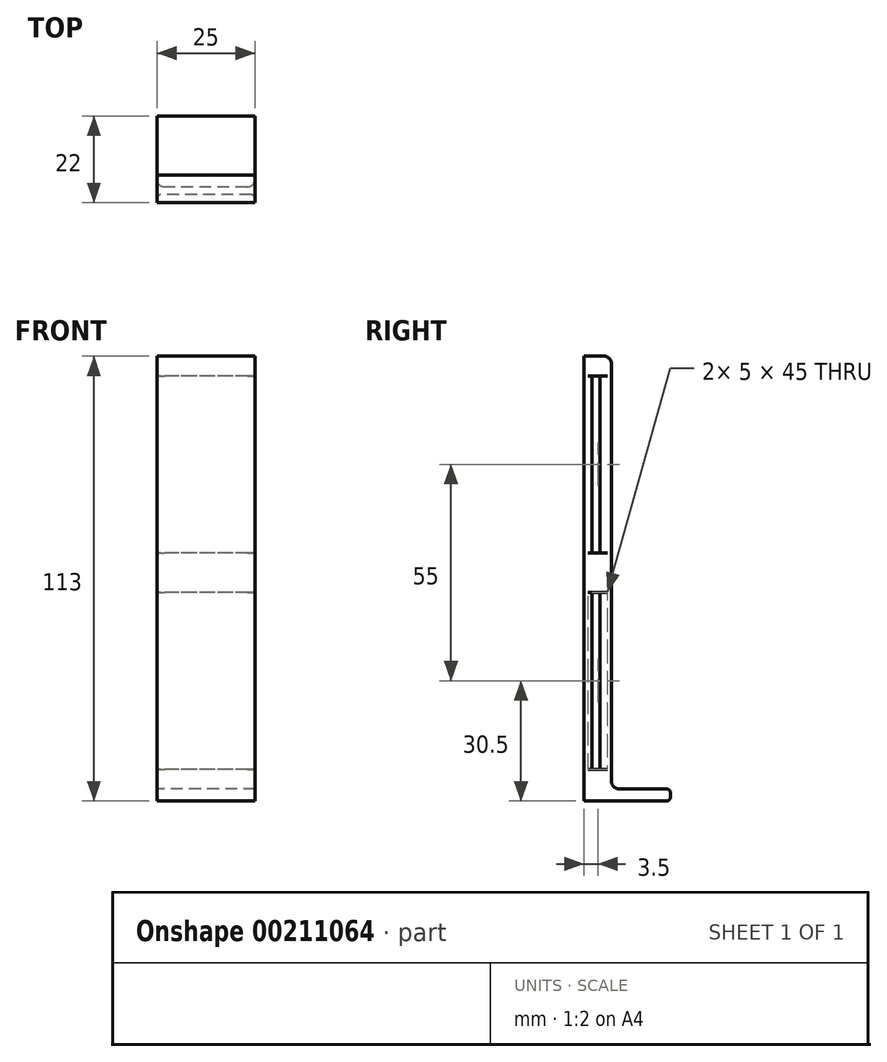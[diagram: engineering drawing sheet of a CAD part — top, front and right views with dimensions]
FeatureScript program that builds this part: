
annotation { "Feature Type Name" : "Feature", "Feature Type Description" : "" }
export const myFeature = defineFeature(function(context is Context, id is Id, definition is map)
    precondition{}
    {
        {
            var Q0;
            Q0=qCreatedBy(makeId("Right.planeOp"),FACE);
            var sketch = newSketch(context, id + "F0", { "sketchPlane" : qUnion([Q0])});
            skLineSegment(sketch, "E0", {"start": v(0, 113) * mm, "end": v(0, 0) * mm});
            skLineSegment(sketch, "E1", {"start": v(0, 0) * mm, "end": v(21, 0) * mm});
            skLineSegment(sketch, "E2", {"start": v(21, 3) * mm, "end": v(7, 3) * mm});
            skLineSegment(sketch, "E3", {"start": v(7, 3) * mm, "end": v(7, 113) * mm});
            skLineSegment(sketch, "E4", {"start": v(7, 113) * mm, "end": v(0, 113) * mm});
            skLineSegment(sketch, "E5.bottom", {"start": v(2, 108) * mm, "end": v(4, 108) * mm});
            skLineSegment(sketch, "E5.top", {"start": v(2, 63) * mm, "end": v(4, 63) * mm});
            skLineSegment(sketch, "E5.left", {"start": v(2, 108) * mm, "end": v(2, 63) * mm});
            skLineSegment(sketch, "E5.right", {"start": v(4, 108) * mm, "end": v(4, 63) * mm});
            skLineSegment(sketch, "E6.bottom", {"start": v(2, 53) * mm, "end": v(4, 53) * mm});
            skLineSegment(sketch, "E6.top", {"start": v(2, 8) * mm, "end": v(4, 8) * mm});
            skLineSegment(sketch, "E6.left", {"start": v(2, 53) * mm, "end": v(2, 8) * mm});
            skLineSegment(sketch, "E6.right", {"start": v(4, 53) * mm, "end": v(4, 8) * mm});
            skLineSegment(sketch, "E7", {"start": v(7, 58) * mm, "end": v(0, 58) * mm, "construction": true});
            skLineSegment(sketch, "E8", {"start": v(22, 1) * mm, "end": v(22, 2) * mm});
            skPoint(sketch, "E9.visualSharp", {"position": v(22, 3) * mm});
            skArc(sketch, "E9.filletArc", {"start": v(22, 2) * mm, "mid": v(21.7, 2.7) * mm, "end": v(21, 3) * mm});
            skPoint(sketch, "E10.visualSharp", {"position": v(22, 0) * mm});
            skArc(sketch, "E10.filletArc", {"start": v(21, 0) * mm, "mid": v(21.7, 0.3) * mm, "end": v(22, 1) * mm});
            skSolve(sketch);
        }
        {
            var Q0;
            Q0=makeQuery(id+"F0.imprint","IMPRINT",FACE,{"disambiguationData":[TD([[makeQuery(id+"F0.imprint","IMPRINT",EDGE,{"derivedFrom":sQuery(id+"F0.wireOp",EDGE,"E0")}),1.0]])]});
            extrude(context, id + "F1", {"entities" : qUnion([Q0]), "depth" : 25 * mm});
        }
        {
            var Q0;
            Q0=makeQuery(id+"F1.opExtrude","SWEPT_EDGE",EDGE,{"disambiguationData":[OSD([sQuery(id+"F0.wireOp",EDGE,"E2"),sQuery(id+"F0.wireOp",EDGE,"E3")])]});
            var Q1;
            Q1=makeQuery(id+"F1.opExtrude","SWEPT_EDGE",EDGE,{"disambiguationData":[OSD([sQuery(id+"F0.wireOp",EDGE,"TeItDx5S-dmeC-bbpO-K6b3-K9wIp6qIZ5ub"),sQuery(id+"F0.wireOp",EDGE,"E2")])]});
            var Q2;
            Q2=makeQuery(id+"F1.opExtrude","SWEPT_EDGE",EDGE,{"disambiguationData":[OSD([sQuery(id+"F0.wireOp",EDGE,"E3"),sQuery(id+"F0.wireOp",EDGE,"E4")])]});
            fillet(context, id + "F2", {"entities" : qUnion([Q0, Q1, Q2]), "radius" : 2 * mm, "tangentPropagation" : true, "allowEdgeOverflow" : false});
        }
        {
            var Q0;
            Q0=makeQuery(id+"F1.opExtrude","CAP_EDGE",EDGE,{"disambiguationData":[OSD([sQuery(id+"F0.wireOp",EDGE,"E5.right")])],"isStart":true});
            var Q1;
            Q1=makeQuery(id+"F1.opExtrude","CAP_EDGE",EDGE,{"disambiguationData":[OSD([sQuery(id+"F0.wireOp",EDGE,"E6.right")])],"isStart":true});
            var Q2;
            Q2=makeQuery(id+"F1.opExtrude","CAP_EDGE",EDGE,{"disambiguationData":[OSD([sQuery(id+"F0.wireOp",EDGE,"E6.right")])],"isStart":false});
            var Q3;
            Q3=makeQuery(id+"F1.opExtrude","CAP_EDGE",EDGE,{"disambiguationData":[OSD([sQuery(id+"F0.wireOp",EDGE,"E5.right")])],"isStart":false});
            fillet(context, id + "F3", {"entities" : qUnion([Q0, Q1, Q2, Q3]), "radius" : 2 * mm, "tangentPropagation" : true, "allowEdgeOverflow" : false});
        }
        {
            var Q0;
            Q0=makeQuery(id+"F1.opExtrude","CAP_EDGE",EDGE,{"disambiguationData":[OSD([sQuery(id+"F0.wireOp",EDGE,"E6.left")])],"isStart":false});
            var Q1;
            Q1=makeQuery(id+"F1.opExtrude","CAP_EDGE",EDGE,{"disambiguationData":[OSD([sQuery(id+"F0.wireOp",EDGE,"E5.left")])],"isStart":false});
            var Q2;
            Q2=makeQuery(id+"F1.opExtrude","CAP_EDGE",EDGE,{"disambiguationData":[OSD([sQuery(id+"F0.wireOp",EDGE,"E5.left")])],"isStart":true});
            var Q3;
            Q3=makeQuery(id+"F1.opExtrude","CAP_EDGE",EDGE,{"disambiguationData":[OSD([sQuery(id+"F0.wireOp",EDGE,"E6.left")])],"isStart":true});
            fillet(context, id + "F4", {"entities" : qUnion([Q0, Q1, Q2, Q3]), "radius" : 1 * mm, "tangentPropagation" : true, "allowEdgeOverflow" : false});
        }
    });
